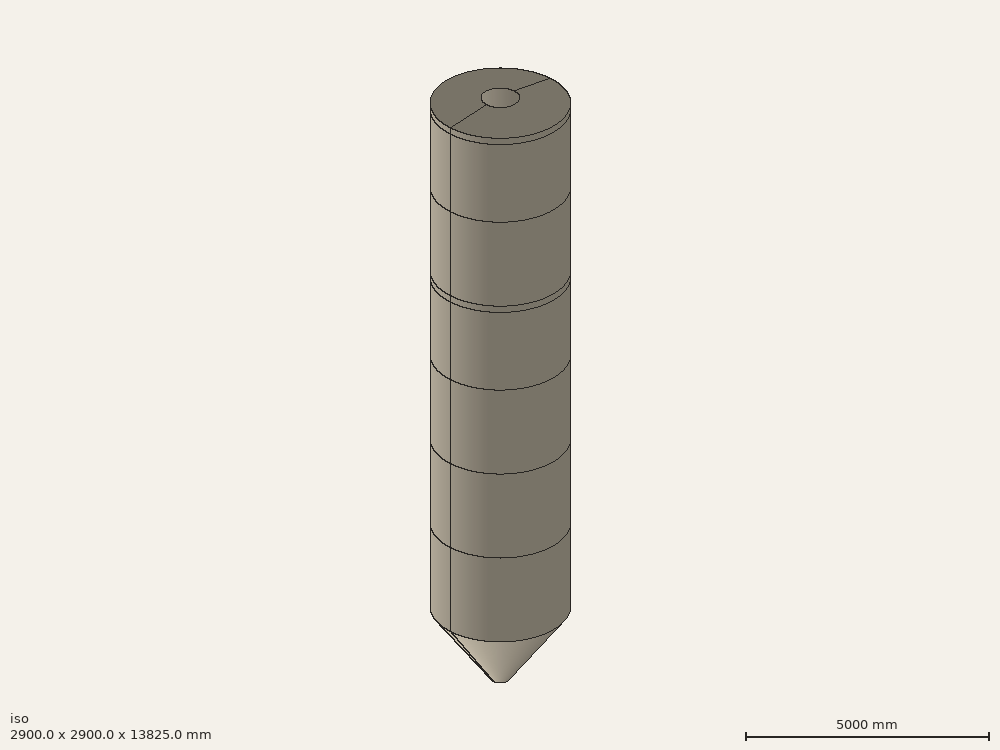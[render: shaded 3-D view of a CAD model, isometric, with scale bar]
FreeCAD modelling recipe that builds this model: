
FCSTD DOCUMENT  (FreeCAD 0.21R33694 (Git))
Label: NMS_Ruhrstr12_Silo_FEM_RC
License: All rights reserved
LicenseURL: http://en.wikipedia.org/wiki/All_rights_reserved
objects: Fem::ConstraintPressure×4, Fem::FeaturePython×3, Image::ImagePlane×1, Sketcher::SketchObject×1, Part::Revolution×1, Part::Mirroring×1, Part::FeaturePython×1, Fem::FemSolverObjectPython×1, App::MaterialObjectPython×1, Fem::ConstraintDisplacement×1, Fem::FemAnalysis×1
note: 4 computed .brp shape members not serialized (recipe doc carries the construction recipe); baked Part::Feature solids carry a one-line shape summary decoded from their .brp

FEATURE [Image::ImagePlane] ImagePlane  label="ansicht"
  Placement = pos=(2598,2000,7284) rot=(-1,0,0;4.71239rad)
  XSize = 20822.6
  YSize = 21481.1
  expr: XSize = 259.33 * 80.294 mm
  expr: YSize = 267.53 * 80.294 mm
FEATURE [Sketcher::SketchObject] Sketch
  FullyConstrained = true
  Placement = pos=(0,0,0) rot=(1,0,0;1.5708rad)
  sketch-geometry (10):
    g0: LineSegment StartX=1450 StartY=4200 StartZ=0 EndX=200 EndY=2500 EndZ=0
    g1: LineSegment StartX=1450 StartY=10200 StartZ=0 EndX=1450 EndY=12050 EndZ=0
    g2: LineSegment StartX=1450 StartY=12050 StartZ=0 EndX=1450 EndY=12200 EndZ=0
    g3: LineSegment StartX=1450 StartY=12200 StartZ=0 EndX=1450 EndY=14200 EndZ=0
    g4: LineSegment StartX=1450 StartY=14200 StartZ=0 EndX=1450 EndY=16050 EndZ=0
    g5: LineSegment StartX=1450 StartY=16050 StartZ=0 EndX=1450 EndY=16200 EndZ=0
    g6: LineSegment StartX=1450 StartY=8200 StartZ=0 EndX=1450 EndY=10200 EndZ=0
    g7: LineSegment StartX=1450 StartY=4200 StartZ=0 EndX=1450 EndY=6200 EndZ=0
    g8: LineSegment StartX=1450 StartY=6200 StartZ=0 EndX=1450 EndY=8200 EndZ=0
    g9: LineSegment StartX=1450 StartY=16200 StartZ=0 EndX=400 EndY=16325 EndZ=0
  constraints (31):
    c: DistanceY(g0,g0) = 1700
    c: DistanceX(g-1,g0) = 200
    c: DistanceX(g-1,g0) = 1450
    c: DistanceY(g0) = 2500
    c: Coincident(g0,g7)
    c: Coincident(g6,g1)
    c: Vertical(g1)
    c: Coincident(g1,g2)
    c: Vertical(g2)
    c: Coincident(g2,g3)
    c: Coincident(g3,g4)
    c: Vertical(g4)
    c: Coincident(g4,g5)
    c: Vertical(g5)
    c: Vertical(g3)
    c: DistanceY(g5,g5) = 150
    c: DistanceY(g3,g5) = 2000
    c: DistanceY(g3,g3) = 2000
    c: Equal(g2,g5)
    c: DistanceY(g6,g2) = 2000
    c: DistanceY(g0,g5) = 12000
    c: Coincident(g8,g6)
    c: Vertical(g6)
    c: Coincident(g7,g8)
    c: Vertical(g7)
    c: Vertical(g8)
    c: Equal(g3,g6)
    c: Equal(g6,g8)
    c: Coincident(g9,g5)
    c: DistanceY(g5,g9) = 125
    c: DistanceX(g-1,g9) = 400
FEATURE [Part::Revolution] Revolve
  Angle = 180
  Axis = (0,0,1)
  Base = (0,0,0)
  FaceMakerClass = Part::FaceMakerBullseye
  Solid = false
  Source = -> Sketch
  Symmetric = false
FEATURE [Part::Mirroring] Part__Mirroring  label="Revolve (Mirror #1)"
  Base = (0,0,0)
  Normal = (0,1,0)
  Source = -> Revolve
FEATURE [Part::FeaturePython] Facebinder  # WARN: FeaturePython — macro-defined, semantics opaque (R4)
  Area = 1.26411e+08
  Extrusion = 0
  Faces = -> [Part__Mirroring,Revolve]
  RemoveSplitter = false
  Sew = false
FEATURE [Fem::FemSolverObjectPython] SolverCcxTools  # FEM object (typed FeaturePython)
  AnalysisType = 0
  BeamReducedIntegration = true
  BeamShellResultOutput3D = true
  BucklingFactors = 3
  EigenmodeHighLimit = 1000000
  EigenmodeLowLimit = 0
  EigenmodesCount = 10
  GeometricalNonlinearity = 0
  IterationsControlParameterCutb = 0.25,0.5,0.75,0.85,,,1.5,
  IterationsControlParameterIter = 4,8,9,200,10,400,,200,,
  IterationsControlParameterTimeUse = false
  IterationsMaximum = 2000
  IterationsThermoMechMaximum = 2000
  IterationsUserDefinedIncrementations = false
  IterationsUserDefinedTimeStepLength = false
  MaterialNonlinearity = 0
  MatrixSolverType = 0
  ModelSpace = 0
  OutputFrequency = 1
  SplitInputWriter = true
  ThermoMechSteadyState = true
  ThermoMechType = 0
  TimeEnd = 1
  TimeInitialStep = 0.01
  TimeMaximumStep = 1
  TimeMinimumStep = 1e-05
FEATURE [App::MaterialObjectPython] MaterialSolid  label="S235"  # material (typed FeaturePython)
  Category = 0
  Material = AmbientColor=(0.0020, 0.0020, 0.0020, 1.0),Author=M. Münch,AuthorAndLicense=LGPL-2.0-or-later,CardName=Steel-S235JR,Density=7850.000000000001 kg/m^3,+18 more (map truncated)
FEATURE [Fem::ConstraintDisplacement] ConstraintDisplacement
  NormalDirection = (0,0,1)
  Normals = (18) [(0,0,1),(0,0,1),(0,0,1),(0,0,1),(0,0,1),(0,0,1),(0,0,1),(0,0,1),(0,0,1),(0,0,1),(0,0,1),(0,0,1),(0,0,1),(0,0,1),(0,0,1),(0,0,1),(0,0,1),(0,0,1)]
  Points = (18) [(1450,9.28e-13,4200),(1339.63,-554.891,4200),(1025.3,-1025.3,4200),(554.891,-1339.63,4200),(1.01679e-12,-1450,4200),(-554.891,-1339.63,4200),+12 more]
  References = -> [Facebinder]
  Scale = 60
  hasXFormula = false
  hasYFormula = false
  hasZFormula = false
  rotxFix = false
  rotxFree = true
  rotyFix = false
  rotyFree = true
  rotzFix = false
  rotzFree = true
  useFlowSurfaceForce = false
  xDisplacement = 0
  xFix = false
  xFree = false
  xRotation = 0
  yDisplacement = 0
  yFix = false
  yFree = false
  yRotation = 0
  zDisplacement = 0
  zFix = false
  zFree = false
  zRotation = 0
FEATURE [Fem::ConstraintPressure] ConstraintPressure
  NormalDirection = (-2.5e-15,1,0)
  Normals = (44) [(-1,-2.46e-15,0),(-0.951057,0.309017,0),(-0.809017,0.587785,0),(-0.587785,0.809017,0),(-0.309017,0.951057,0),(-2.52123e-15,1,0),(0.309017,0.951057,0),+37 more]
  Points = (44) [(1450,3.567e-12,16050),(1379.03,-448.075,16050),(1173.07,-852.289,16050),(852.289,-1173.07,16050),(448.075,-1379.03,16050),(3.65579e-12,-1450,16050),+38 more]
  Pressure = 1e-06
  References = -> [Facebinder]
  Reversed = true
  Scale = 47
FEATURE [Fem::ConstraintPressure] ConstraintPressure001
  NormalDirection = (-2.5e-15,-1,0)
  Normals = (44) [(-1,2.46e-15,0),(-0.951057,-0.309017,0),(-0.809017,-0.587785,0),(-0.587785,-0.809017,0),(-0.309017,-0.951057,0),(-2.52123e-15,-1,0),+38 more]
  Points = (44) [(1450,-3.567e-12,16050),(1379.03,448.075,16050),(1173.07,852.289,16050),(852.289,1173.07,16050),(448.075,1379.03,16050),(3.65579e-12,1450,16050),+38 more]
  Pressure = 1e-06
  References = -> [Facebinder]
  Reversed = true
  Scale = 47
FEATURE [Fem::ConstraintPressure] ConstraintPressure002
  NormalDirection = (-1.9e-15,1,0)
  Normals = (44) [(-1,-1.85e-15,0),(-0.951057,0.309017,0),(-0.809017,0.587785,0),(-0.587785,0.809017,0),(-0.309017,0.951057,0),(-1.91123e-15,1,0),(0.309017,0.951057,0),+37 more]
  Points = (44) [(1450,2.6825e-12,12050),(1379.03,-448.075,12050),(1173.07,-852.289,12050),(852.289,-1173.07,12050),(448.075,-1379.03,12050),(2.77129e-12,-1450,12050),+38 more]
  Pressure = 0.1
  References = -> [Facebinder]
  Reversed = true
  Scale = 47
FEATURE [Fem::ConstraintPressure] ConstraintPressure003
  NormalDirection = (-1.9e-15,-1,0)
  Normals = (44) [(-1,1.85e-15,0),(-0.951057,-0.309017,0),(-0.809017,-0.587785,0),(-0.587785,-0.809017,0),(-0.309017,-0.951057,0),(-1.91123e-15,-1,0),+38 more]
  Points = (44) [(1450,-2.6825e-12,12050),(1379.03,448.075,12050),(1173.07,852.289,12050),(852.289,1173.07,12050),(448.075,1379.03,12050),(2.77129e-12,1450,12050),+38 more]
  Pressure = 0.1
  References = -> [Facebinder]
  Reversed = true
  Scale = 47
FEATURE [Fem::FeaturePython] ElementGeometry2D  label="4mm"  # FEM object (typed FeaturePython)
  References = -> [Facebinder]
  Thickness = 4
FEATURE [Fem::FeaturePython] MeshRegion  # FEM object (typed FeaturePython)
  CharacteristicLength = 40
  References = -> [Facebinder]
FEATURE [Fem::FeaturePython] ElementGeometry2D001  label="5mm"  # FEM object (typed FeaturePython)
  References = -> [Facebinder]
  Thickness = 5
FEATURE [Fem::FemAnalysis] Analysis
  Group = -> [SolverCcxTools,MaterialSolid,ConstraintDisplacement,ConstraintPressure,ConstraintPressure001,ConstraintPressure002,ConstraintPressure003,ElementGeometry2D,ElementGeometry2D001]
